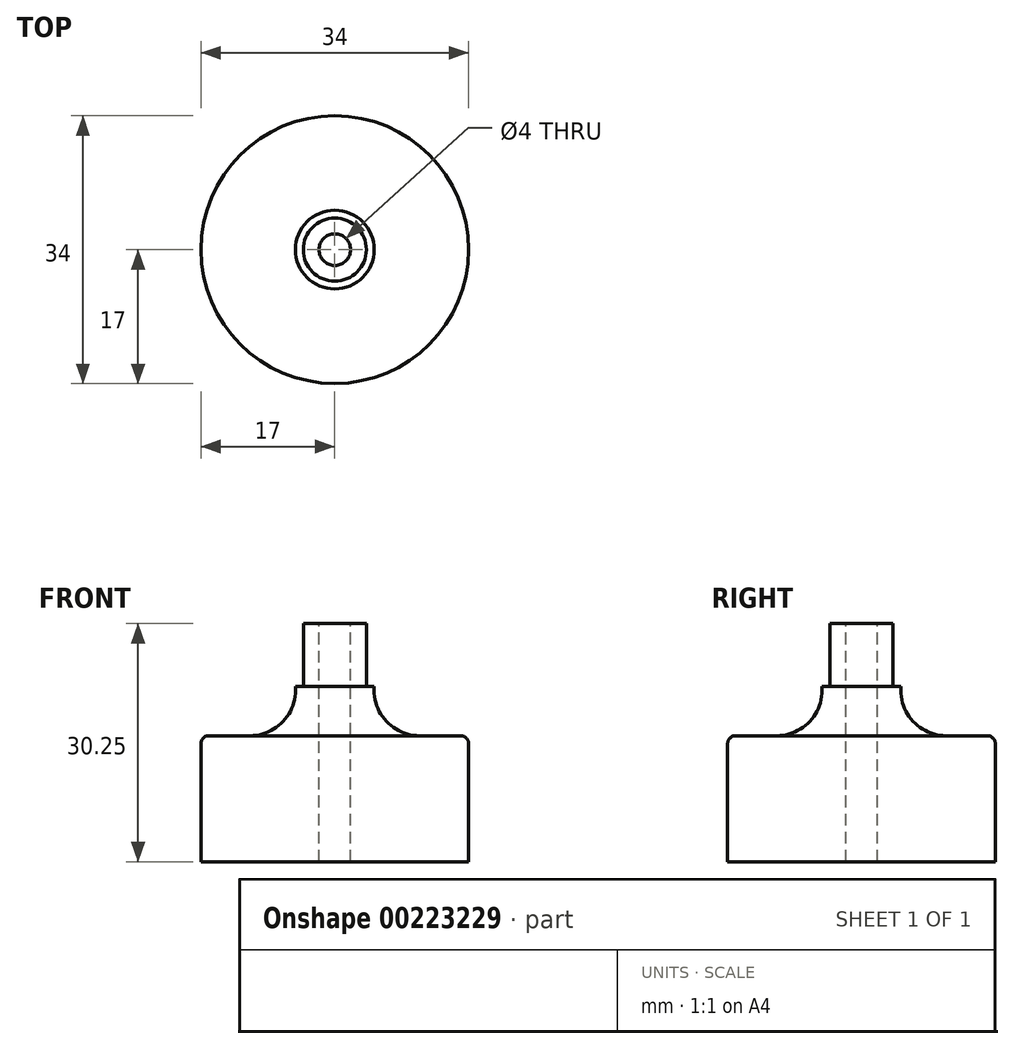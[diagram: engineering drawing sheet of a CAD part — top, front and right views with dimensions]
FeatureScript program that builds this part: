
annotation { "Feature Type Name" : "Feature", "Feature Type Description" : "" }
export const myFeature = defineFeature(function(context is Context, id is Id, definition is map)
    precondition{}
    {
        {
            var Q0;
            Q0=qCreatedBy(makeId("Front.planeOp"),FACE);
            var sketch = newSketch(context, id + "F0", { "sketchPlane" : qUnion([Q0])});
            skLineSegment(sketch, "E0", {"start": v(0, 30.25) * mm, "end": v(0, 0) * mm, "construction": true});
            skLineSegment(sketch, "E1", {"start": v(-17, 0) * mm, "end": v(-17, 15) * mm});
            skLineSegment(sketch, "E2.0", {"start": v(-17, 0) * mm, "end": v(-2, 0) * mm});
            skLineSegment(sketch, "E3.0", {"start": v(-4, 30.25) * mm, "end": v(-2, 30.25) * mm});
            skLineSegment(sketch, "E4", {"start": v(-4, 30.25) * mm, "end": v(-4, 22.25) * mm});
            skLineSegment(sketch, "E5", {"start": v(-4, 22.25) * mm, "end": v(-5, 22.25) * mm});
            skLineSegment(sketch, "E6.0", {"start": v(-5, 22.25) * mm, "end": v(-4, 22.25) * mm});
            skLineSegment(sketch, "E7", {"start": v(-5, 22.25) * mm, "end": v(-5, 21.75) * mm});
            skArc(sketch, "E8", {"start": v(-10.75, 16) * mm, "mid": v(-6.68, 17.68) * mm, "end": v(-5, 21.75) * mm});
            skLineSegment(sketch, "E9", {"start": v(-10.75, 16) * mm, "end": v(-16, 16) * mm});
            skArc(sketch, "E10", {"start": v(-16, 16) * mm, "mid": v(-16.7, 15.7) * mm, "end": v(-17, 15) * mm});
            skLineSegment(sketch, "E11", {"start": v(-2, 30.25) * mm, "end": v(-2, 0) * mm});
            skSolve(sketch);
        }
        {
            var Q0;
            Q0=makeQuery(id+"F0.imprint","IMPRINT",FACE,{"disambiguationData":[TD([[makeQuery(id+"F0.imprint","IMPRINT",EDGE,{"derivedFrom":sQuery(id+"F0.wireOp",EDGE,"E1")}),-1.0]])]});
            var Q1;
            Q1=sQuery(id+"F0.wireOp",EDGE,"E0");
            revolve(context, id + "F1", {"entities" : qUnion([Q0]), "axis" : qUnion([Q1]), "revolveType" : RevolveType.FULL});
        }
    });
